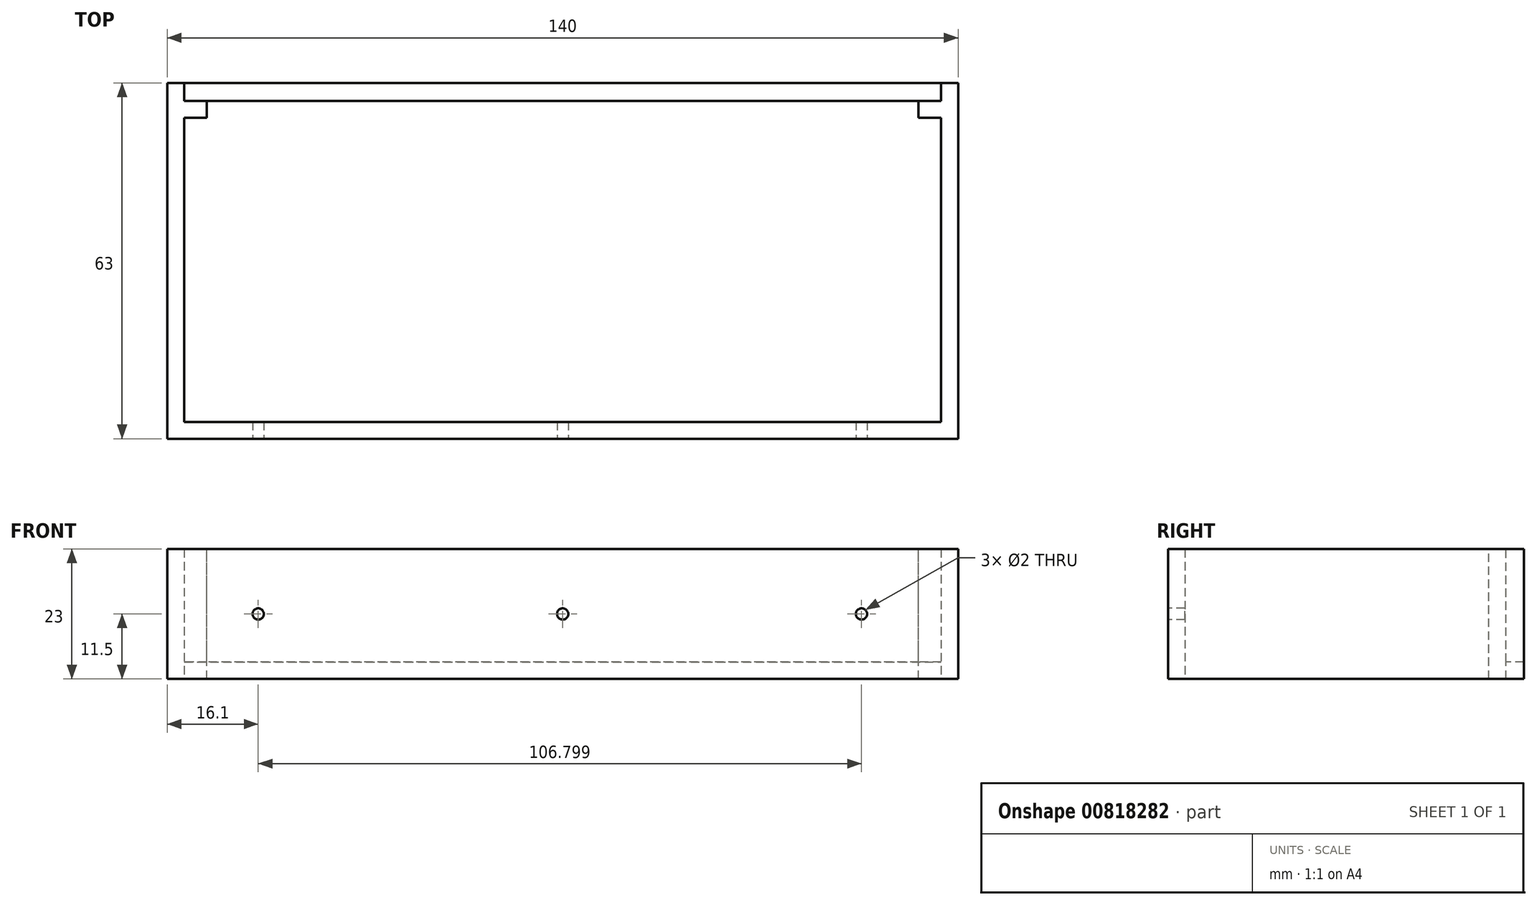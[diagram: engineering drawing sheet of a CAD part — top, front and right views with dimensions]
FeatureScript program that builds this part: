
annotation { "Feature Type Name" : "Feature", "Feature Type Description" : "" }
export const myFeature = defineFeature(function(context is Context, id is Id, definition is map)
    precondition{}
    {
        {
            var Q0;
            Q0=qCreatedBy(makeId("Top.planeOp"),FACE);
            var sketch = newSketch(context, id + "F0", { "sketchPlane" : qUnion([Q0])});
            skLineSegment(sketch, "E0.bottom", {"start": v(-80, 33.03) * mm, "end": v(60, 33.03) * mm});
            skLineSegment(sketch, "E0.top", {"start": v(-80, -32.97) * mm, "end": v(60, -32.97) * mm});
            skLineSegment(sketch, "E0.left", {"start": v(-80, 33.03) * mm, "end": v(-80, -32.97) * mm});
            skLineSegment(sketch, "E0.right", {"start": v(60, 33.03) * mm, "end": v(60, -32.97) * mm});
            skLineSegment(sketch, "E1.left", {"start": v(-80, -32.97) * mm, "end": v(-80, 0.03) * mm});
            skLineSegment(sketch, "E1.right", {"start": v(60, -9.97) * mm, "end": v(60, 0.03) * mm});
            skLineSegment(sketch, "E2.bottom", {"start": v(-80, -32.97) * mm, "end": v(-45, -32.97) * mm});
            skLineSegment(sketch, "E2.top", {"start": v(-80, 33.03) * mm, "end": v(-60, 33.03) * mm});
            skLineSegment(sketch, "E2.left", {"start": v(-80, -32.97) * mm, "end": v(-80, 33.03) * mm});
            skLineSegment(sketch, "E3.bottom", {"start": v(-45, -32.97) * mm, "end": v(-25, -32.97) * mm});
            skLineSegment(sketch, "E3.top", {"start": v(-60, 33.03) * mm, "end": v(-40, 33.03) * mm});
            skLineSegment(sketch, "E4.bottom", {"start": v(-25, -32.97) * mm, "end": v(-5, -32.97) * mm});
            skLineSegment(sketch, "E4.top", {"start": v(-40, 33.03) * mm, "end": v(-20, 33.03) * mm});
            skPoint(sketch, "E5.oppositeSnap0", {"position": v(-10, 33.03) * mm});
            skLineSegment(sketch, "E5.bottom", {"start": v(-5, -32.97) * mm, "end": v(15, -32.97) * mm});
            skLineSegment(sketch, "E5.top", {"start": v(-20, 33.03) * mm, "end": v(0, 33.03) * mm});
            skLineSegment(sketch, "E6.bottom", {"start": v(15, -32.97) * mm, "end": v(35, -32.97) * mm});
            skLineSegment(sketch, "E6.top", {"start": v(0, 33.03) * mm, "end": v(20, 33.03) * mm});
            skLineSegment(sketch, "E7.bottom", {"start": v(35, -32.97) * mm, "end": v(55, -32.97) * mm});
            skLineSegment(sketch, "E7.top", {"start": v(20, 33.03) * mm, "end": v(40, 33.03) * mm});
            skLineSegment(sketch, "E8.left", {"start": v(-80, -32.97) * mm, "end": v(-80, -2.97) * mm});
            skLineSegment(sketch, "E8.right", {"start": v(60, -24.97) * mm, "end": v(60, -4.97) * mm});
            skLineSegment(sketch, "E9.left", {"start": v(-80, 33.03) * mm, "end": v(-80, 18.03) * mm});
            skLineSegment(sketch, "E9.right", {"start": v(60, 33.03) * mm, "end": v(60, 18.03) * mm});
            skCircle(sketch, "E10", {"center": v(-45, 1.03) * mm, "radius": 8 * mm});
            skCircle(sketch, "E11", {"center": v(25, -0.47) * mm, "radius": 8 * mm});
            skLineSegment(sketch, "E12.left", {"start": v(-80, -32.97) * mm, "end": v(-80, -17.97) * mm});
            skLineSegment(sketch, "E12.right", {"start": v(60, -32.97) * mm, "end": v(60, -14.97) * mm});
            skLineSegment(sketch, "E13.top", {"start": v(-80, -29.97) * mm, "end": v(60, -29.97) * mm});
            skLineSegment(sketch, "E13.left", {"start": v(-80, -32.97) * mm, "end": v(-80, -29.97) * mm});
            skLineSegment(sketch, "E13.right", {"start": v(60, -32.97) * mm, "end": v(60, -29.97) * mm});
            skSolve(sketch);
        }
        {
            var Q0;
            Q0=makeQuery(id+"F0.imprint","IMPRINT",FACE,{"disambiguationData":[TD([[makeQuery(id+"F0.imprint","IMPRINT",EDGE,{"derivedFrom":sQuery(id+"F0.wireOp",EDGE,"E0.right")}),-1.0]])]});
            extrude(context, id + "F1", {"entities" : qUnion([Q0]), "depth" : 3 * mm, "offsetDistance" : 25 * mm});
        }
        {
            var Q0;
            Q0=makeQuery(id+"F1.opExtrude","CAP_FACE",FACE,{"disambiguationData":[OSD([sQuery(id+"F0.wireOp",EDGE,"E0.right"),sQuery(id+"F0.wireOp",EDGE,"E1.right"),sQuery(id+"F0.wireOp",EDGE,"E2.left"),sQuery(id+"F0.wireOp",EDGE,"E8.left"),sQuery(id+"F0.wireOp",EDGE,"E8.right"),sQuery(id+"F0.wireOp",EDGE,"E0.bottom"),sQuery(id+"F0.wireOp",EDGE,"E9.left"),sQuery(id+"F0.wireOp",EDGE,"E9.right"),sQuery(id+"F0.wireOp",EDGE,"l78r6zbi-zdNL-ogfi-jeJ1-84AOC1EXPDmI"),sQuery(id+"F0.wireOp",EDGE,"7xFXzIXv-dOzj-SHI9-m5NP-5MGqcVb28G0k"),sQuery(id+"F0.wireOp",EDGE,"E10"),sQuery(id+"F0.wireOp",EDGE,"k8Uu2vQ0-tXef-bBox-vRSx-lKBiwxJhI1xb"),sQuery(id+"F0.wireOp",EDGE,"E11"),sQuery(id+"F0.wireOp",EDGE,"5OqNOj1d-C8S8-WuIc-Ppvz-3VOTpNMQOR2k"),sQuery(id+"F0.wireOp",EDGE,"E12.left"),sQuery(id+"F0.wireOp",EDGE,"E12.right"),sQuery(id+"F0.wireOp",EDGE,"HoM0chx2-d7kJ-X9MT-WdqG-gqhH9dmnozYe"),sQuery(id+"F0.wireOp",EDGE,"JgkcrWLJ-2lYI-B5tP-8zwM-9y0SQbQCKJUD"),sQuery(id+"F0.wireOp",EDGE,"uQcqgJcq-6ofs-f9DD-1k3D-WOd607GN4n9v"),sQuery(id+"F0.wireOp",EDGE,"E13.top")])],"isStart":false});
            var sketch = newSketch(context, id + "F2", { "sketchPlane" : qUnion([Q0])});
            skLineSegment(sketch, "E14.bottom", {"start": v(-80, -29.97) * mm, "end": v(60, -29.97) * mm});
            skLineSegment(sketch, "E14.top", {"start": v(-80, -26.97) * mm, "end": v(60, -26.97) * mm});
            skLineSegment(sketch, "E14.left", {"start": v(-80, -29.97) * mm, "end": v(-80, -26.97) * mm});
            skLineSegment(sketch, "E14.right", {"start": v(60, -29.97) * mm, "end": v(60, -26.97) * mm});
            skLineSegment(sketch, "E15.left", {"start": v(-80, 33.03) * mm, "end": v(-80, 30.03) * mm});
            skLineSegment(sketch, "E15.right", {"start": v(60, 33.03) * mm, "end": v(60, 30.03) * mm});
            skLineSegment(sketch, "E16.bottom", {"start": v(-80, 33.03) * mm, "end": v(-77, 33.03) * mm});
            skLineSegment(sketch, "E16.top", {"start": v(-80, -29.97) * mm, "end": v(-77, -29.97) * mm});
            skLineSegment(sketch, "E16.left", {"start": v(-80, 33.03) * mm, "end": v(-80, -29.97) * mm});
            skLineSegment(sketch, "E16.right", {"start": v(-77, 33.03) * mm, "end": v(-77, -29.97) * mm});
            skLineSegment(sketch, "E17.bottom", {"start": v(60, 33.03) * mm, "end": v(57, 33.03) * mm});
            skLineSegment(sketch, "E17.top", {"start": v(60, -29.97) * mm, "end": v(57, -29.97) * mm});
            skLineSegment(sketch, "E17.left", {"start": v(60, 33.03) * mm, "end": v(60, -29.97) * mm});
            skLineSegment(sketch, "E17.right", {"start": v(57, 33.03) * mm, "end": v(57, -29.97) * mm});
            skSolve(sketch);
        }
        {
            var Q0;
            Q0=qSketchRegion(id+"F2",true);
            extrude(context, id + "F3", {"entities" : qUnion([Q0]), "operationType" : NewBodyOperationType.ADD, "depth" : 20 * mm, "offsetDistance" : 25 * mm});
        }
        {
            var Q0;
            Q0=makeQuery(id+"F3.opExtrude","SWEPT_FACE",FACE,{"disambiguationData":[OSD([sQuery(id+"F2.wireOp",EDGE,"E16.right")])]});
            var sketch = newSketch(context, id + "F4", { "sketchPlane" : qUnion([Q0])});
            skLineSegment(sketch, "E18.bottom", {"start": v(33.03, 23) * mm, "end": v(29.83, 23) * mm});
            skLineSegment(sketch, "E18.top", {"start": v(33.03, 3) * mm, "end": v(29.83, 3) * mm});
            skLineSegment(sketch, "E18.left", {"start": v(33.03, 23) * mm, "end": v(33.03, 3) * mm});
            skLineSegment(sketch, "E18.right", {"start": v(29.83, 23) * mm, "end": v(29.83, 3) * mm});
            skLineSegment(sketch, "E19.bottom", {"start": v(29.83, 23) * mm, "end": v(26.83, 23) * mm});
            skLineSegment(sketch, "E19.top", {"start": v(29.83, 3) * mm, "end": v(26.83, 3) * mm});
            skLineSegment(sketch, "E19.right", {"start": v(26.83, 23) * mm, "end": v(26.83, 3) * mm});
            skSolve(sketch);
        }
        {
            var Q0;
            Q0=makeQuery(id+"F4.imprint","IMPRINT",FACE,{"disambiguationData":[TD([[makeQuery(id+"F4.imprint","IMPRINT",EDGE,{"derivedFrom":sQuery(id+"F4.wireOp",EDGE,"E19.bottom")}),1.0]])]});
            extrude(context, id + "F5", {"entities" : qUnion([Q0]), "operationType" : NewBodyOperationType.ADD, "depth" : 134 * mm, "offsetDistance" : 25 * mm});
        }
        {
            var Q0;
            Q0=makeQuery(id+"F5.boolean.opBoolean","MERGE",FACE,{"derivedFrom":[makeQuery(id+"F3.opExtrude","CAP_FACE",FACE,{"disambiguationData":[OSD([sQuery(id+"F2.wireOp",EDGE,"E14.bottom"),sQuery(id+"F2.wireOp",EDGE,"E14.top"),sQuery(id+"F2.wireOp",EDGE,"E16.bottom"),sQuery(id+"F2.wireOp",EDGE,"E16.top"),sQuery(id+"F2.wireOp",EDGE,"E16.left"),sQuery(id+"F2.wireOp",EDGE,"E16.right"),sQuery(id+"F2.wireOp",EDGE,"E17.bottom"),sQuery(id+"F2.wireOp",EDGE,"E17.top"),sQuery(id+"F2.wireOp",EDGE,"E17.left"),sQuery(id+"F2.wireOp",EDGE,"E17.right")])],"isStart":false}),makeQuery(id+"F5.opExtrude","SWEPT_FACE",FACE,{"disambiguationData":[OSD([sQuery(id+"F4.wireOp",EDGE,"E19.bottom")])]})]});
            var sketch = newSketch(context, id + "F6", { "sketchPlane" : qUnion([Q0])});
            skLineSegment(sketch, "E20.bottom", {"start": v(-73, 29.83) * mm, "end": v(53, 29.83) * mm});
            skLineSegment(sketch, "E20.top", {"start": v(-73, 26.83) * mm, "end": v(53, 26.83) * mm});
            skLineSegment(sketch, "E20.left", {"start": v(-73, 29.83) * mm, "end": v(-73, 26.83) * mm});
            skLineSegment(sketch, "E20.right", {"start": v(53, 29.83) * mm, "end": v(53, 26.83) * mm});
            skSolve(sketch);
        }
        {
            var Q0;
            Q0=qSketchRegion(id+"F6",true);
            extrude(context, id + "F7", {"entities" : qUnion([Q0]), "operationType" : NewBodyOperationType.REMOVE, "oppositeDirection" : true, "depth" : 40 * mm, "offsetDistance" : 25 * mm});
        }
        {
            var Q0;
            Q0=makeQuery(id+"F3.opExtrude","SWEPT_FACE",FACE,{"disambiguationData":[OSD([sQuery(id+"F2.wireOp",EDGE,"E14.top")])]});
            var sketch = newSketch(context, id + "F8", { "sketchPlane" : qUnion([Q0])});
            skLineSegment(sketch, "E21.bottom", {"start": v(77, 23) * mm, "end": v(-57, 23) * mm});
            skLineSegment(sketch, "E21.left", {"start": v(77, 23) * mm, "end": v(77, 6.99) * mm});
            skLineSegment(sketch, "E21.right", {"start": v(-57, 26.99) * mm, "end": v(-57, 23) * mm});
            skCircle(sketch, "E22", {"center": v(47, 26.99) * mm, "radius": 1.5 * mm});
            skCircle(sketch, "E23", {"center": v(-27, 26.99) * mm, "radius": 1.5 * mm});
            skCircle(sketch, "E24", {"center": v(10, 26.99) * mm, "radius": 1.5 * mm});
            skSolve(sketch);
        }
        {
            var Q0;
            Q0=makeQuery(id+"F8.imprint","IMPRINT",FACE,{"disambiguationData":[TD([[makeQuery(id+"F8.imprint","IMPRINT",EDGE,{"derivedFrom":sQuery(id+"F8.wireOp",EDGE,"E22")}),1.0]])]});
            var Q1;
            Q1=makeQuery(id+"F8.imprint","IMPRINT",FACE,{"disambiguationData":[TD([[makeQuery(id+"F8.imprint","IMPRINT",EDGE,{"derivedFrom":sQuery(id+"F8.wireOp",EDGE,"E23")}),1.0]])]});
            var Q2;
            Q2=makeQuery(id+"F8.imprint","IMPRINT",FACE,{"disambiguationData":[TD([[makeQuery(id+"F8.imprint","IMPRINT",EDGE,{"derivedFrom":sQuery(id+"F8.wireOp",EDGE,"E24")}),1.0]])]});
            extrude(context, id + "F9", {"entities" : qUnion([Q0, Q1, Q2]), "operationType" : NewBodyOperationType.REMOVE, "oppositeDirection" : true, "depth" : 3 * mm, "offsetDistance" : 25 * mm});
        }
        {
            var Q0;
            {var subQ1=sQuery(id+"F0.wireOp",EDGE,"E0.bottom");var subQ3=sQuery(id+"F0.wireOp",EDGE,"E11");var subQ4=sQuery(id+"F0.wireOp",EDGE,"E10");var subQ5=makeQuery(id+"F1.opExtrude","CAP_FACE",FACE,{"disambiguationData":[OSD([sQuery(id+"F0.wireOp",EDGE,"E0.right"),sQuery(id+"F0.wireOp",EDGE,"E1.right"),sQuery(id+"F0.wireOp",EDGE,"E2.left"),sQuery(id+"F0.wireOp",EDGE,"E8.left"),sQuery(id+"F0.wireOp",EDGE,"E8.right"),subQ1,sQuery(id+"F0.wireOp",EDGE,"E9.left"),sQuery(id+"F0.wireOp",EDGE,"E9.right"),subQ4,subQ3,sQuery(id+"F0.wireOp",EDGE,"E12.left"),sQuery(id+"F0.wireOp",EDGE,"E12.right"),sQuery(id+"F0.wireOp",EDGE,"E13.top")])],"isStart":false});Q0=makeQuery(id+"F7.boolean.opBoolean","MERGE",FACE,{"derivedFrom":[makeQuery(id+"F5.boolean.opBoolean","SPLIT",FACE,{"disambiguationData":[TD([makeQuery(id+"F1.opExtrude","SWEPT_FACE",FACE,{"disambiguationData":[OSD([subQ4])]})])],"derivedFrom":subQ5}),makeQuery(id+"F5.boolean.opBoolean","SPLIT",FACE,{"disambiguationData":[TD([makeQuery(id+"F1.opExtrude","SWEPT_FACE",FACE,{"disambiguationData":[OSD([subQ1])]})])],"derivedFrom":subQ5}),makeQuery(id+"F7.opExtrude","CAP_FACE",FACE,{"disambiguationData":[OSD([sQuery(id+"F6.wireOp",EDGE,"E20.bottom"),sQuery(id+"F6.wireOp",EDGE,"E20.top"),sQuery(id+"F6.wireOp",EDGE,"E20.left"),sQuery(id+"F6.wireOp",EDGE,"E20.right")])],"isStart":false})]});}
            var sketch = newSketch(context, id + "F10", { "sketchPlane" : qUnion([Q0])});
            skSolve(sketch);
        }
        {
            var Q0;
            {var subQ3=sQuery(id+"F0.wireOp",EDGE,"E10");Q0=makeQuery(id+"F10.imprint","IMPRINT",FACE,{"disambiguationData":[TD([[makeQuery(id+"F10.imprint","IMPRINT",EDGE,{"derivedFrom":makeQuery(id+"F1.opExtrude","CAP_EDGE",EDGE,{"disambiguationData":[OSD([subQ3])],"isStart":false})}),-1.0]])]});}
            var sketch = newSketch(context, id + "F11", { "sketchPlane" : qUnion([Q0])});
            skSolve(sketch);
        }
        {
            var Q0;
            Q0=qSketchRegion(id+"F11",true);
            var Q1;
            {var subQ3=sQuery(id+"F0.wireOp",EDGE,"E10");Q1=makeQuery(id+"F10.imprint","IMPRINT",FACE,{"disambiguationData":[TD([[makeQuery(id+"F10.imprint","IMPRINT",EDGE,{"derivedFrom":makeQuery(id+"F1.opExtrude","CAP_EDGE",EDGE,{"disambiguationData":[OSD([subQ3])],"isStart":false})}),-1.0]])]});}
            extrude(context, id + "F12", {"entities" : qUnion([Q0, Q1]), "operationType" : NewBodyOperationType.REMOVE, "oppositeDirection" : true, "depth" : 40 * mm, "offsetDistance" : 25 * mm});
        }
        {
            var Q0;
            Q0=makeQuery(id+"F3.boolean.opBoolean","MERGE",FACE,{"derivedFrom":[makeQuery(id+"F1.opExtrude","SWEPT_FACE",FACE,{"disambiguationData":[OSD([sQuery(id+"F0.wireOp",EDGE,"E13.top")])]}),makeQuery(id+"F3.opExtrude","SWEPT_FACE",FACE,{"disambiguationData":[OSD([sQuery(id+"F2.wireOp",EDGE,"E14.bottom"),sQuery(id+"F2.wireOp",EDGE,"E16.top"),sQuery(id+"F2.wireOp",EDGE,"E17.top")])]})]});
            var sketch = newSketch(context, id + "F13", { "sketchPlane" : qUnion([Q0])});
            skCircle(sketch, "E25", {"center": v(-63.9, 11.5) * mm, "radius": 1 * mm});
            skCircle(sketch, "E26", {"center": v(-10, 11.5) * mm, "radius": 1 * mm});
            skCircle(sketch, "E27", {"center": v(42.9, 11.5) * mm, "radius": 1 * mm});
            skSolve(sketch);
        }
        {
            var Q0;
            Q0 = qSketchRegion(id + "F13", true);
            extrude(context, id + "F14", {"entities" : qUnion([Q0]), "operationType" : NewBodyOperationType.REMOVE, "oppositeDirection" : true, "depth" : 3 * mm, "offsetDistance" : 25 * mm});
        }
    });
